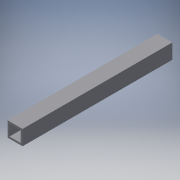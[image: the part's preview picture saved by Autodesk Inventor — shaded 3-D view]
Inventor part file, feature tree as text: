
AUTODESK INVENTOR PART (.ipt)
format: ipt  version: 2016 (Build 200138000, 138)  size: 92,672 bytes
history: native  units: in
note: dims shown in document units (in); Inventor stores cm internally (conversion verified against a paired STEP export)
features: extrude x1, sketch x1
ambient origin geometry x8: Origin, YZ Plane, XZ Plane, XY Plane, X Axis, Y Axis, Z Axis, Center Point
bodies: Solid1 (feature_tree)
feature tree (2):
  extrude  "Extrusion1"  Depth=1.0in
  sketch  "Sketch1"  dims[d0=1.0in d1=1.0in d2=0.125in d3=10.0in d4=0.0in]
